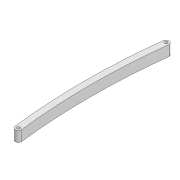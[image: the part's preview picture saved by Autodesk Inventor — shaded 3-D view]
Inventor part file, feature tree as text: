
AUTODESK INVENTOR PART (.ipt)
format: ipt  version: 2022 (Build 260153000, 153)  size: 90,624 bytes
history: native  units: mm
features: extrude x1, sketch x1
ambient origin geometry x8: Origin, YZ Plane, XZ Plane, XY Plane, X Axis, Y Axis, Z Axis, Center Point
bodies: Solid1 (feature_tree)
feature tree (2):
  extrude  "Extrusion1"  Depth=141.096mm
  sketch  "Sketch1"  dims[d0=6.0mm d1=141.096mm d2=3.0mm d3=3.0mm d4=10.0mm d5=0.0mm d10=600.0mm d11=600.0mm]
